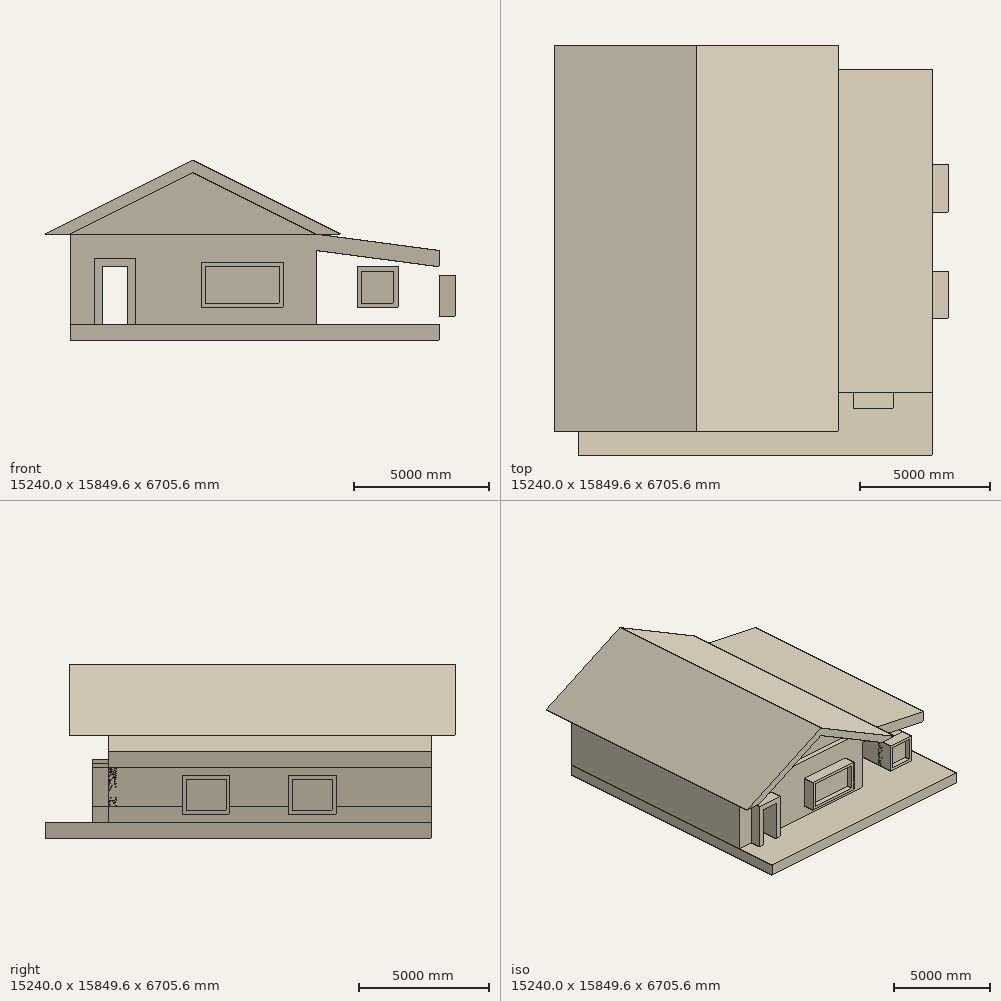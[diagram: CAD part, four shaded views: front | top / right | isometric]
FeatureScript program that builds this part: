
annotation { "Feature Type Name" : "Feature", "Feature Type Description" : "" }
export const myFeature = defineFeature(function(context is Context, id is Id, definition is map)
    precondition{}
    {
        {
            var Q0;
            Q0=qCreatedBy(makeId("Front.planeOp"),FACE);
            var sketch = newSketch(context, id + "F0", { "sketchPlane" : qUnion([Q0])});
            skLineSegment(sketch, "E0", {"start": v(0, 0) * mm, "end": v(-4572, 0) * mm});
            skLineSegment(sketch, "E1", {"start": v(-4572, 0) * mm, "end": v(4572, 0) * mm});
            skLineSegment(sketch, "E2.top", {"start": v(-4572, -3352.8) * mm, "end": v(4572, -3352.8) * mm});
            skLineSegment(sketch, "E2.left", {"start": v(-4572, 0) * mm, "end": v(-4572, -3352.8) * mm});
            skLineSegment(sketch, "E2.right", {"start": v(4572, 0) * mm, "end": v(4572, -3352.8) * mm});
            skLineSegment(sketch, "E3", {"start": v(0, 0) * mm, "end": v(0, 2286) * mm, "construction": true});
            skLineSegment(sketch, "E4", {"start": v(0, 2286) * mm, "end": v(-4572, 0) * mm});
            skLineSegment(sketch, "E5", {"start": v(0, 2286) * mm, "end": v(4572, 0) * mm});
            skLineSegment(sketch, "E6", {"start": v(-4572, 0) * mm, "end": v(-5486.4, 0) * mm});
            skLineSegment(sketch, "E7", {"start": v(0, 2286) * mm, "end": v(0, 2743.2) * mm, "construction": true});
            skLineSegment(sketch, "E8", {"start": v(-5486.4, 0) * mm, "end": v(0, 2743.2) * mm});
            skLineSegment(sketch, "E9", {"start": v(4572, 0) * mm, "end": v(5486.4, 0) * mm});
            skLineSegment(sketch, "E10", {"start": v(5486.4, 0) * mm, "end": v(0, 2743.2) * mm});
            skLineSegment(sketch, "E11", {"start": v(4572, -3352.8) * mm, "end": v(9144, -3352.8) * mm});
            skLineSegment(sketch, "E12.bottom", {"start": v(-4572, -3352.8) * mm, "end": v(9144, -3352.8) * mm});
            skLineSegment(sketch, "E12.top", {"start": v(-4572, -3962.4) * mm, "end": v(9144, -3962.4) * mm});
            skLineSegment(sketch, "E12.left", {"start": v(-4572, -3352.8) * mm, "end": v(-4572, -3962.4) * mm});
            skLineSegment(sketch, "E12.right", {"start": v(9144, -3352.8) * mm, "end": v(9144, -3962.4) * mm});
            skLineSegment(sketch, "E13.bottom", {"start": v(-3352.8, -3352.8) * mm, "end": v(-2438.4, -3352.8) * mm});
            skLineSegment(sketch, "E13.top", {"start": v(-3352.8, -1219.2) * mm, "end": v(-2438.4, -1219.2) * mm});
            skLineSegment(sketch, "E13.left", {"start": v(-3352.8, -3352.8) * mm, "end": v(-3352.8, -1219.2) * mm});
            skLineSegment(sketch, "E13.right", {"start": v(-2438.4, -3352.8) * mm, "end": v(-2438.4, -1219.2) * mm});
            skLineSegment(sketch, "E14", {"start": v(4572, 0) * mm, "end": v(4572, -609.6) * mm});
            skLineSegment(sketch, "E15", {"start": v(9144, -3352.8) * mm, "end": v(9144, -609.6) * mm});
            skLineSegment(sketch, "E16", {"start": v(4572, -609.6) * mm, "end": v(9144, -1212.83) * mm});
            skLineSegment(sketch, "E17", {"start": v(9144, -609.6) * mm, "end": v(4572, 0) * mm});
            skLineSegment(sketch, "E18.0", {"start": v(-2133.6, -3352.8) * mm, "end": v(-2133.6, -914.4) * mm});
            skLineSegment(sketch, "E18.1", {"start": v(-3657.6, -914.4) * mm, "end": v(-2133.6, -914.4) * mm});
            skLineSegment(sketch, "E18.2", {"start": v(-3657.6, -3352.8) * mm, "end": v(-3657.6, -914.4) * mm});
            skLineSegment(sketch, "E19.bottom", {"start": v(457.2, -1219.2) * mm, "end": v(3200.4, -1219.2) * mm});
            skLineSegment(sketch, "E19.top", {"start": v(457.2, -2590.8) * mm, "end": v(3200.4, -2590.8) * mm});
            skLineSegment(sketch, "E19.left", {"start": v(457.2, -1219.2) * mm, "end": v(457.2, -2590.8) * mm});
            skLineSegment(sketch, "E19.right", {"start": v(3200.4, -1219.2) * mm, "end": v(3200.4, -2590.8) * mm});
            skLineSegment(sketch, "E20.0", {"start": v(304.8, -1066.8) * mm, "end": v(304.8, -2743.2) * mm});
            skLineSegment(sketch, "E20.1", {"start": v(304.8, -1066.8) * mm, "end": v(3352.8, -1066.8) * mm});
            skLineSegment(sketch, "E20.2", {"start": v(3352.8, -1066.8) * mm, "end": v(3352.8, -2743.2) * mm});
            skLineSegment(sketch, "E20.3", {"start": v(304.8, -2743.2) * mm, "end": v(3352.8, -2743.2) * mm});
            skLineSegment(sketch, "E21.bottom", {"start": v(6248.4, -2590.8) * mm, "end": v(7467.6, -2590.8) * mm});
            skLineSegment(sketch, "E21.top", {"start": v(6248.4, -1371.6) * mm, "end": v(7467.6, -1371.6) * mm});
            skLineSegment(sketch, "E21.left", {"start": v(6248.4, -2590.8) * mm, "end": v(6248.4, -1371.6) * mm});
            skLineSegment(sketch, "E21.right", {"start": v(7467.6, -2590.8) * mm, "end": v(7467.6, -1371.6) * mm});
            skLineSegment(sketch, "E22.0", {"start": v(6096, -1219.2) * mm, "end": v(7620, -1219.2) * mm});
            skLineSegment(sketch, "E22.1", {"start": v(6096, -2743.2) * mm, "end": v(6096, -1219.2) * mm});
            skLineSegment(sketch, "E22.2", {"start": v(6096, -2743.2) * mm, "end": v(7620, -2743.2) * mm});
            skLineSegment(sketch, "E22.3", {"start": v(7620, -2743.2) * mm, "end": v(7620, -1219.2) * mm});
            skText(sketch, "E23", { "text": "Property of Elizabeth", "fontName": "OpenSans-Bold.ttf"});
            const initialGuessF0  = {"E23": [-3.1102, 5.05076, 1, 0, 0.56553]};
            skSetInitialGuess(sketch, initialGuessF0);
            skSolve(sketch);
        }
        {
            var Q0;
            Q0=makeQuery(id+"F0.imprint","IMPRINT",FACE,{"disambiguationData":[TD([[makeQuery(id+"F0.imprint","IMPRINT",EDGE,{"derivedFrom":sQuery(id+"F0.wireOp",EDGE,"E4")}),-1.0]])]});
            var Q1;
            Q1=makeQuery(id+"F0.imprint","IMPRINT",FACE,{"disambiguationData":[TD([[makeQuery(id+"F0.imprint","IMPRINT",EDGE,{"derivedFrom":sQuery(id+"F0.wireOp",EDGE,"E14")}),1.0]])]});
            extrude(context, id + "F1", {"entities" : qUnion([Q0, Q1]), "depth" : 1828.8 * mm, "offsetDistance" : 30.48 * mm, "hasSecondDirection" : true, "secondDirectionOppositeDirection" : true, "secondDirectionDepth" : 13106.4 * mm});
        }
        {
            var Q0;
            {var subQ0=sQuery(id+"F0.wireOp",EDGE,"E4");Q0=makeQuery(id+"F0.imprint","IMPRINT",FACE,{"disambiguationData":[TD([[makeQuery(id+"F0.imprint","IMPRINT",EDGE,{"derivedFrom":subQ0}),1.0]])]});}
            extrude(context, id + "F2", {"entities" : qUnion([Q0]), "operationType" : NewBodyOperationType.ADD, "oppositeDirection" : true, "depth" : 12192 * mm, "offsetDistance" : 30.48 * mm});
        }
        {
            var Q0;
            Q0=makeQuery(id+"F0.imprint","IMPRINT",FACE,{"disambiguationData":[TD([[makeQuery(id+"F0.imprint","IMPRINT",EDGE,{"derivedFrom":sQuery(id+"F0.wireOp",EDGE,"E13.top")}),1.0]])]});
            var Q1;
            Q1=makeQuery(id+"F0.imprint","IMPRINT",FACE,{"disambiguationData":[TD([[makeQuery(id+"F0.imprint","IMPRINT",EDGE,{"derivedFrom":sQuery(id+"F0.wireOp",EDGE,"E13.bottom")}),1.0]])]});
            var Q2;
            {var subQ3=sQuery(id+"F0.wireOp",EDGE,"E2.left");Q2=makeQuery(id+"F0.imprint","IMPRINT",FACE,{"disambiguationData":[TD([[makeQuery(id+"F0.imprint","IMPRINT",EDGE,{"derivedFrom":subQ3}),1.0]])]});}
            var Q3;
            Q3=makeQuery(id+"F0.imprint","IMPRINT",FACE,{"disambiguationData":[TD([[makeQuery(id+"F0.imprint","IMPRINT",EDGE,{"derivedFrom":sQuery(id+"F0.wireOp",EDGE,"E19.bottom")}),-1.0]])]});
            var Q4;
            Q4=makeQuery(id+"F0.imprint","IMPRINT",FACE,{"disambiguationData":[TD([[makeQuery(id+"F0.imprint","IMPRINT",EDGE,{"derivedFrom":sQuery(id+"F0.wireOp",EDGE,"E21.bottom")}),1.0]])]});
            var Q5;
            Q5=makeQuery(id+"F0.imprint","IMPRINT",FACE,{"disambiguationData":[TD([[makeQuery(id+"F0.imprint","IMPRINT",EDGE,{"derivedFrom":sQuery(id+"F0.wireOp",EDGE,"E19.bottom")}),1.0]])]});
            var Q6;
            Q6=makeQuery(id+"F0.imprint","IMPRINT",FACE,{"disambiguationData":[TD([[makeQuery(id+"F0.imprint","IMPRINT",EDGE,{"derivedFrom":sQuery(id+"F0.wireOp",EDGE,"E21.bottom")}),-1.0]])]});
            var Q7;
            {var subQ2=sQuery(id+"F0.wireOp",EDGE,"E2.right");Q7=makeQuery(id+"F0.imprint","IMPRINT",FACE,{"disambiguationData":[TD([[makeQuery(id+"F0.imprint","IMPRINT",EDGE,{"derivedFrom":subQ2}),1.0]])]});}
            extrude(context, id + "F3", {"entities" : qUnion([Q0, Q1, Q2, Q3, Q4, Q5, Q6, Q7]), "depth" : 304.8 * mm, "offsetDistance" : 30.48 * mm, "hasSecondDirection" : true, "secondDirectionOppositeDirection" : true, "secondDirectionDepth" : 12192 * mm});
        }
        {
            var Q0;
            Q0=makeQuery(id+"F0.imprint","IMPRINT",FACE,{"disambiguationData":[TD([[makeQuery(id+"F0.imprint","IMPRINT",EDGE,{"derivedFrom":sQuery(id+"F0.wireOp",EDGE,"E12.top")}),1.0]])]});
            extrude(context, id + "F4", {"entities" : qUnion([Q0]), "depth" : 2743.2 * mm, "offsetDistance" : 30.48 * mm, "hasSecondDirection" : true, "secondDirectionOppositeDirection" : true, "secondDirectionDepth" : 12192 * mm});
        }
        {
            var Q0;
            Q0=makeQuery(id+"F0.imprint","IMPRINT",FACE,{"disambiguationData":[TD([[makeQuery(id+"F0.imprint","IMPRINT",EDGE,{"derivedFrom":sQuery(id+"F0.wireOp",EDGE,"E13.bottom")}),1.0]])]});
            var Q1;
            Q1=makeQuery(id+"F0.imprint","IMPRINT",FACE,{"disambiguationData":[TD([[makeQuery(id+"F0.imprint","IMPRINT",EDGE,{"derivedFrom":sQuery(id+"F0.wireOp",EDGE,"E19.bottom")}),-1.0]])]});
            var Q2;
            Q2=makeQuery(id+"F0.imprint","IMPRINT",FACE,{"disambiguationData":[TD([[makeQuery(id+"F0.imprint","IMPRINT",EDGE,{"derivedFrom":sQuery(id+"F0.wireOp",EDGE,"E21.bottom")}),1.0]])]});
            extrude(context, id + "F5", {"entities" : qUnion([Q0, Q1, Q2]), "depth" : 609.6 * mm, "offsetDistance" : 30.48 * mm});
        }
        {
            var Q0;
            Q0=makeQuery(id+"F0.imprint","IMPRINT",FACE,{"disambiguationData":[TD([[makeQuery(id+"F0.imprint","IMPRINT",EDGE,{"derivedFrom":sQuery(id+"F0.wireOp",EDGE,"E13.top")}),1.0]])]});
            var Q1;
            Q1=makeQuery(id+"F0.imprint","IMPRINT",FACE,{"disambiguationData":[TD([[makeQuery(id+"F0.imprint","IMPRINT",EDGE,{"derivedFrom":sQuery(id+"F0.wireOp",EDGE,"E19.bottom")}),1.0]])]});
            var Q2;
            Q2=makeQuery(id+"F0.imprint","IMPRINT",FACE,{"disambiguationData":[TD([[makeQuery(id+"F0.imprint","IMPRINT",EDGE,{"derivedFrom":sQuery(id+"F0.wireOp",EDGE,"E21.bottom")}),-1.0]])]});
            extrude(context, id + "F6", {"entities" : qUnion([Q0, Q1, Q2]), "depth" : 914.4 * mm, "offsetDistance" : 30.48 * mm});
        }
        {
            var Q0;
            Q0=makeQuery(id+"F3.opExtrude","SWEPT_FACE",FACE,{"disambiguationData":[OSD([sQuery(id+"F0.wireOp",EDGE,"E15")])]});
            var sketch = newSketch(context, id + "F7", { "sketchPlane" : qUnion([Q0])});
            skLineSegment(sketch, "E24.bottom", {"start": v(2710.63, -1674.26) * mm, "end": v(4234.63, -1674.26) * mm});
            skLineSegment(sketch, "E24.top", {"start": v(2710.63, -2893.46) * mm, "end": v(4234.63, -2893.46) * mm});
            skLineSegment(sketch, "E24.left", {"start": v(2710.63, -1674.26) * mm, "end": v(2710.63, -2893.46) * mm});
            skLineSegment(sketch, "E24.right", {"start": v(4234.63, -1674.26) * mm, "end": v(4234.63, -2893.46) * mm});
            skLineSegment(sketch, "E25.bottom", {"start": v(6815.27, -1674.26) * mm, "end": v(8339.27, -1674.26) * mm});
            skLineSegment(sketch, "E25.top", {"start": v(6815.27, -2893.46) * mm, "end": v(8339.27, -2893.46) * mm});
            skLineSegment(sketch, "E25.left", {"start": v(6815.27, -1674.26) * mm, "end": v(6815.27, -2893.46) * mm});
            skLineSegment(sketch, "E25.right", {"start": v(8339.27, -1674.26) * mm, "end": v(8339.27, -2893.46) * mm});
            skLineSegment(sketch, "E26.0", {"start": v(2558.23, -1521.86) * mm, "end": v(4387.03, -1521.86) * mm});
            skLineSegment(sketch, "E26.1", {"start": v(2558.23, -1521.86) * mm, "end": v(2558.23, -3045.86) * mm});
            skLineSegment(sketch, "E26.2", {"start": v(2558.23, -3045.86) * mm, "end": v(4387.03, -3045.86) * mm});
            skLineSegment(sketch, "E26.3", {"start": v(4387.03, -1521.86) * mm, "end": v(4387.03, -3045.86) * mm});
            skLineSegment(sketch, "E27.0", {"start": v(6662.87, -1521.86) * mm, "end": v(8491.67, -1521.86) * mm});
            skLineSegment(sketch, "E27.1", {"start": v(6662.87, -1521.86) * mm, "end": v(6662.87, -3045.86) * mm});
            skLineSegment(sketch, "E27.2", {"start": v(6662.87, -3045.86) * mm, "end": v(8491.67, -3045.86) * mm});
            skLineSegment(sketch, "E27.3", {"start": v(8491.67, -1521.86) * mm, "end": v(8491.67, -3045.86) * mm});
            skSolve(sketch);
        }
        {
            var Q0;
            Q0=makeQuery(id+"F7.imprint","IMPRINT",FACE,{"disambiguationData":[TD([[makeQuery(id+"F7.imprint","IMPRINT",EDGE,{"derivedFrom":sQuery(id+"F7.wireOp",EDGE,"E25.bottom")}),-1.0]])]});
            var Q1;
            Q1=makeQuery(id+"F7.imprint","IMPRINT",FACE,{"disambiguationData":[TD([[makeQuery(id+"F7.imprint","IMPRINT",EDGE,{"derivedFrom":sQuery(id+"F7.wireOp",EDGE,"E24.bottom")}),-1.0]])]});
            extrude(context, id + "F8", {"entities" : qUnion([Q0, Q1]), "depth" : 304.8 * mm, "offsetDistance" : 30.48 * mm});
        }
        {
            var Q0;
            Q0=makeQuery(id+"F7.imprint","IMPRINT",FACE,{"disambiguationData":[TD([[makeQuery(id+"F7.imprint","IMPRINT",EDGE,{"derivedFrom":sQuery(id+"F7.wireOp",EDGE,"E24.bottom")}),1.0]])]});
            var Q1;
            Q1=makeQuery(id+"F7.imprint","IMPRINT",FACE,{"disambiguationData":[TD([[makeQuery(id+"F7.imprint","IMPRINT",EDGE,{"derivedFrom":sQuery(id+"F7.wireOp",EDGE,"E25.bottom")}),1.0]])]});
            extrude(context, id + "F9", {"entities" : qUnion([Q0, Q1]), "depth" : 609.6 * mm, "offsetDistance" : 30.48 * mm});
        }
    });
